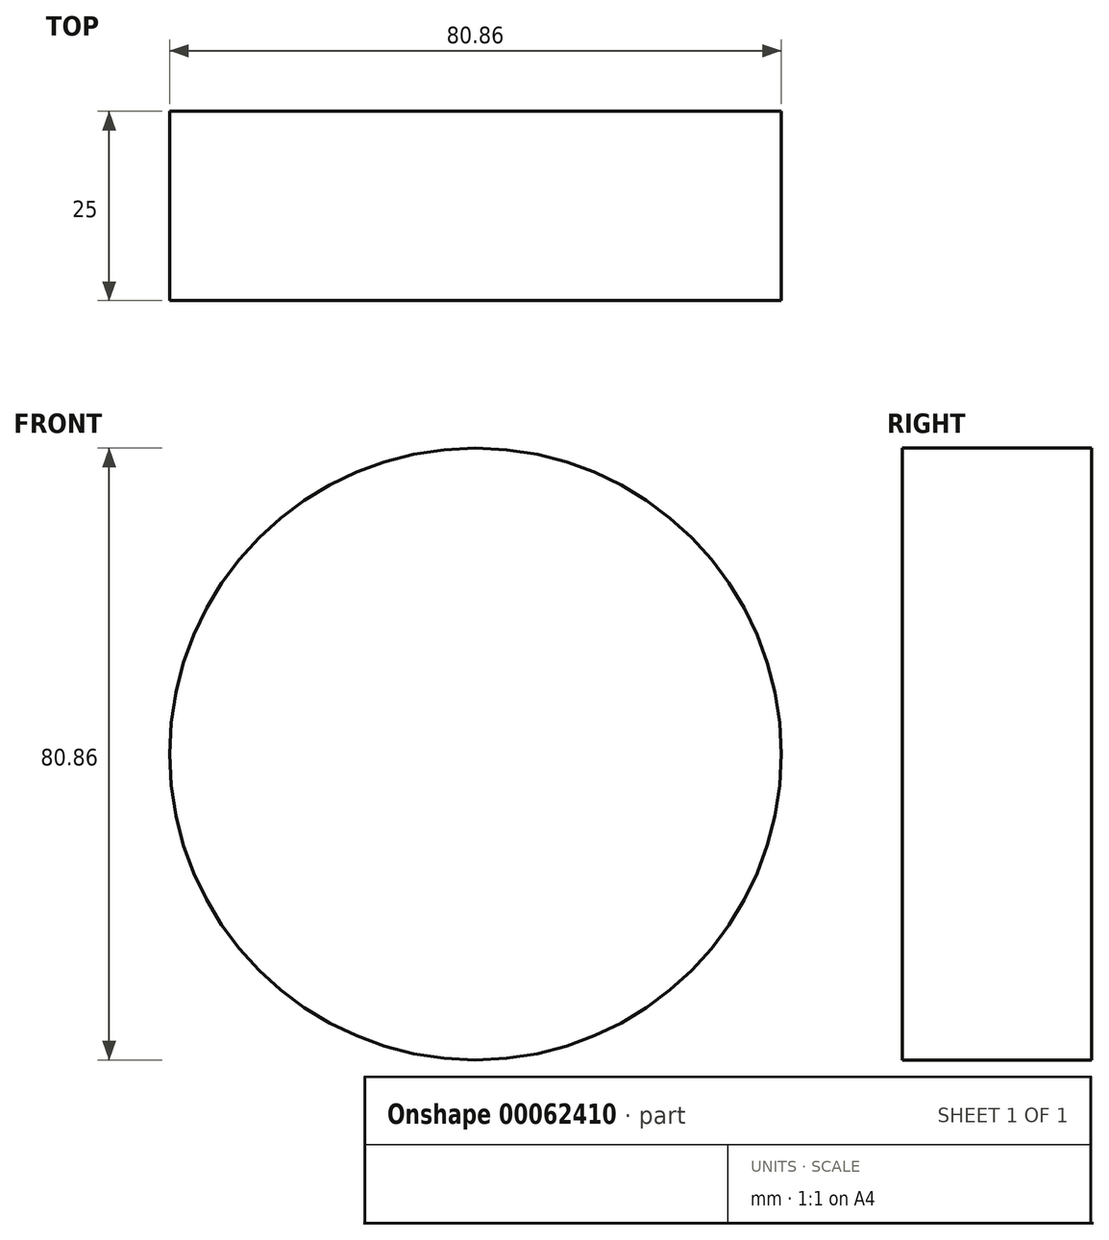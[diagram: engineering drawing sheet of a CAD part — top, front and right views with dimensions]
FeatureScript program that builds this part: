
annotation { "Feature Type Name" : "Feature", "Feature Type Description" : "" }
export const myFeature = defineFeature(function(context is Context, id is Id, definition is map)
    precondition{}
    {
        {
            var Q0;
            Q0=qCreatedBy(makeId("Front.planeOp"),FACE);
            var sketch = newSketch(context, id + "F0", { "sketchPlane" : qUnion([Q0])});
            skCircle(sketch, "E0", {"center": v(0, 0) * mm, "radius": 40.43 * mm});
            skSolve(sketch);
        }
        {
            var Q0;
            Q0=makeQuery(id+"F0.imprint","IMPRINT",FACE,{"disambiguationData":[TD([[makeQuery(id+"F0.imprint","IMPRINT",EDGE,{"derivedFrom":sQuery(id+"F0.wireOp",EDGE,"E0")}),1.0]])]});
            extrude(context, id + "F1", {"entities" : qUnion([Q0]), "depth" : 25 * mm});
        }
    });
